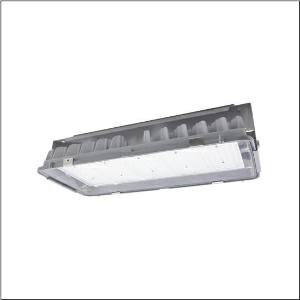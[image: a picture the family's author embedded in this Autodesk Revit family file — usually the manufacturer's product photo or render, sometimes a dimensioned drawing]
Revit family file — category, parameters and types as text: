
# Revit family: highbay_11xtreme_51hf81da4nma
name_source: partatom
category: Lighting Fixtures
units: mm (PartAtom-declared; Revit-internal decimal feet)

## family parameters
Cut with Voids When Loaded = No
Host = Face
Light Source = No
Part Type = Normal
Room Calculation Point = No
Round Connector Dimension = Use Diameter
Shared = No

## types (1)
- --- (1 x LED, 34200 lm, 188.1 W, 4000K)
    Apparent Load = 188 VA
    CIE Flux Codes = 88 96 99 100 100
    Color Rendering = 80
    Color Temperature = 4000K
    Default Elevation = 1800 mm
    Description = Highbay 11Xtreme, LED high bay luminaire, primary light control with lens, of PMMA, primary optical cover: cover, of toughened safety glass, light emission: direct distribution, primary light characteristic: symmetric, installation type: suspended mounting, surface-mounted, 1x LED module,for 1x LED, rated luminous flux: 34.200lm, luminous efficacy: 182lm/W, light colour: 840, colour temperature: 4000K, with cable H07RN-F 5x 1.5mm², mains connection: 220..240V, AC, 50/60Hz, cable length: 1,5m, rated input power: 188W, luminaire housing, of diecast aluminium, partly coated, silver, length: 595mm, width: 280mm, height: 195mm, protection rating (complete): IP66, insulation class (complete): insulation class I (protective earthing), certification: CE, ENEC, UKCA, protection symbol: D, ball protection: ball impact resistant according to DIN VDE 0710 part 13 (with chain suspension), impact resistance: IK08, permissible operating ambient temperature: -25..+45°C, reducing of maximum allowable ambient temperature of 5°C with ceiling mounting, packaging unit: 1 piece
    Height = 157 mm
    Lamp = 1 x LED
    Lamp Light Flux = 34200 lm
    Lamp Power = 188.1 W
    Lamp count = 1
    Length = 593 mm
    Luminous efficacy = 182 lm/W
    Manufacturer = Siteco
    ModVariant = No
    Model = 51HF81DA4NMA
    Mounting Place = Ceiling
    Mounting Type = Pendant
    Number of Poles = 1
    OnlyDefault = Yes
    Power Factor = 1
    Product Name = Highbay 11Xtreme
    Product group = LED high bay luminaire
    ProductGroupID = 903
    Protection Class = Protection class I
    Protection Degree = IP 66
    RLX_Detail_Level = 1
    RLX_Emergency_Light_Flux = 0 lm
    RLX_Emergency_Type = 0
    RLX_Emergency_Type_DB = No
    RlxData = <blob elided: 27841 chars, md5=327fe848>
    Socket = socket
    Standby Power = 0 W
    System Light Flux = 34200 lm
    System Power = 188 W
    Type Comments = factory setting: luminous flux: 100 % | dim-lin: 254 | 1258 mA
    Type Image = l_1258342.jpg
    URL = http://relux.com
    VarID = @adj_035965
    Voltage = 0 V
    Weight = 0.00 kg
    Width = 278 mm

## geometry (parser evidence)
native form markers: Blend x4, Sweep x12
no freeform markers — native parametric forms only
